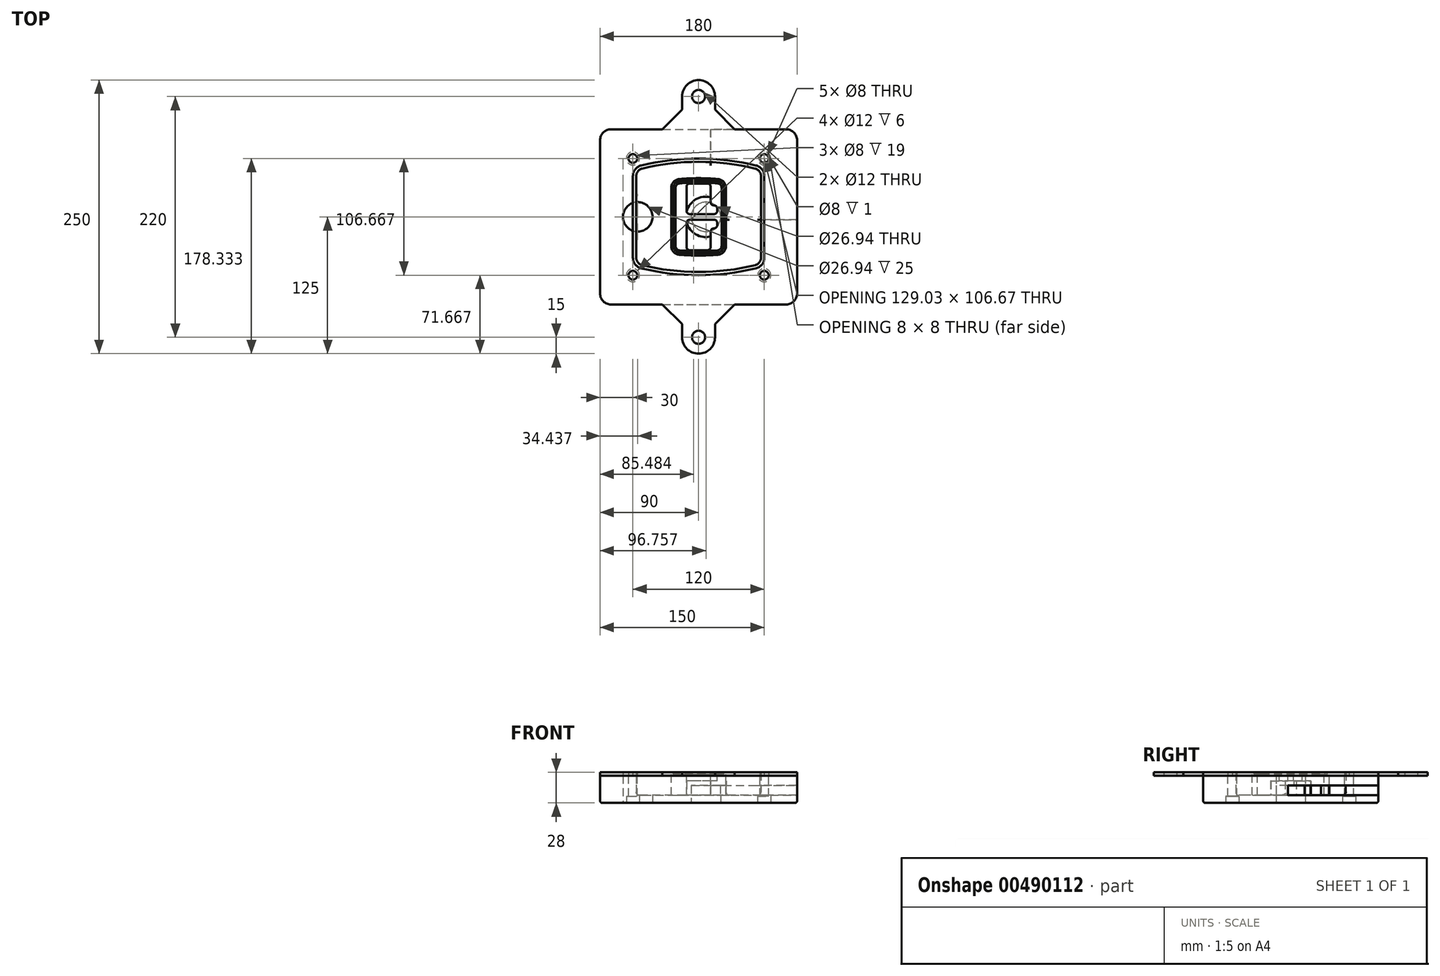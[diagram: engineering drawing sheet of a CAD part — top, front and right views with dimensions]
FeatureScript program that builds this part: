
annotation { "Feature Type Name" : "Feature", "Feature Type Description" : "" }
export const myFeature = defineFeature(function(context is Context, id is Id, definition is map)
    precondition{}
    {
        {
            var Q0;
            Q0=qCreatedBy(makeId("Top.planeOp"),FACE);
            var sketch = newSketch(context, id + "F0", { "sketchPlane" : qUnion([Q0])});
            skPoint(sketch, "E0.rect.middle", {"position": v(0, 0) * mm});
            skLineSegment(sketch, "E1.bottom", {"start": v(-80, -80) * mm, "end": v(80, -80) * mm});
            skLineSegment(sketch, "E1.top", {"start": v(-80, 80) * mm, "end": v(80, 80) * mm});
            skLineSegment(sketch, "E1.left", {"start": v(-90, -70) * mm, "end": v(-90, 70) * mm});
            skLineSegment(sketch, "E1.right", {"start": v(90, -70) * mm, "end": v(90, 70) * mm});
            skLineSegment(sketch, "E2", {"start": v(-90, 80) * mm, "end": v(90, -80) * mm, "construction": true});
            skLineSegment(sketch, "E3", {"start": v(90, 80) * mm, "end": v(-90, -80) * mm, "construction": true});
            skCircle(sketch, "E4", {"center": v(-60, 53.33) * mm, "radius": 4 * mm});
            skCircle(sketch, "E5", {"center": v(60, 53.33) * mm, "radius": 4 * mm});
            skCircle(sketch, "E6", {"center": v(60, -53.33) * mm, "radius": 4 * mm});
            skCircle(sketch, "E7", {"center": v(-60, -53.33) * mm, "radius": 4 * mm});
            skLineSegment(sketch, "E8", {"start": v(-60, 53.33) * mm, "end": v(60, 53.33) * mm, "construction": true});
            skLineSegment(sketch, "E9", {"start": v(60, 53.33) * mm, "end": v(60, -53.33) * mm, "construction": true});
            skLineSegment(sketch, "E10", {"start": v(60, -53.33) * mm, "end": v(-60, -53.33) * mm, "construction": true});
            skLineSegment(sketch, "E11", {"start": v(-60, -53.33) * mm, "end": v(-60, 53.33) * mm, "construction": true});
            skLineSegment(sketch, "E12", {"start": v(-60, 37.3) * mm, "end": v(-60, -37.3) * mm});
            skLineSegment(sketch, "E13", {"start": v(60, 37.3) * mm, "end": v(60, -37.3) * mm});
            skArc(sketch, "E14", {"start": v(52.38, 47.01) * mm, "mid": v(0, 53.33) * mm, "end": v(-52.38, 47.01) * mm});
            skArc(sketch, "E15", {"start": v(-52.38, -47.01) * mm, "mid": v(0, -53.33) * mm, "end": v(52.38, -47.01) * mm});
            skLineSegment(sketch, "E16", {"start": v(-60, 0) * mm, "end": v(60, 0) * mm, "construction": true});
            skPoint(sketch, "E17.visualSharp", {"position": v(-60, -45) * mm});
            skArc(sketch, "E17.filletArc", {"start": v(-60, -37.3) * mm, "mid": v(-57.87, -43.47) * mm, "end": v(-52.38, -47.01) * mm});
            skPoint(sketch, "E18.visualSharp", {"position": v(-60, 45) * mm});
            skArc(sketch, "E18.filletArc", {"start": v(-52.38, 47.01) * mm, "mid": v(-57.87, 43.47) * mm, "end": v(-60, 37.3) * mm});
            skPoint(sketch, "E19.visualSharp", {"position": v(60, 45) * mm});
            skArc(sketch, "E19.filletArc", {"start": v(60, 37.3) * mm, "mid": v(57.87, 43.47) * mm, "end": v(52.38, 47.01) * mm});
            skPoint(sketch, "E20.visualSharp", {"position": v(60, -45) * mm});
            skArc(sketch, "E20.filletArc", {"start": v(52.38, -47.01) * mm, "mid": v(57.87, -43.47) * mm, "end": v(60, -37.3) * mm});
            skPoint(sketch, "E21.visualSharp", {"position": v(-90, 80) * mm});
            skArc(sketch, "E21.filletArc", {"start": v(-80, 80) * mm, "mid": v(-87.07, 77.07) * mm, "end": v(-90, 70) * mm});
            skPoint(sketch, "E22.visualSharp", {"position": v(90, 80) * mm});
            skArc(sketch, "E22.filletArc", {"start": v(90, 70) * mm, "mid": v(87.07, 77.07) * mm, "end": v(80, 80) * mm});
            skPoint(sketch, "E23.visualSharp", {"position": v(90, -80) * mm});
            skArc(sketch, "E23.filletArc", {"start": v(80, -80) * mm, "mid": v(87.07, -77.07) * mm, "end": v(90, -70) * mm});
            skPoint(sketch, "E24.visualSharp", {"position": v(-90, -80) * mm});
            skArc(sketch, "E24.filletArc", {"start": v(-90, -70) * mm, "mid": v(-87.07, -77.07) * mm, "end": v(-80, -80) * mm});
            skArc(sketch, "E25.0", {"start": v(57, 37.3) * mm, "mid": v(55.5, 41.62) * mm, "end": v(51.67, 44.1) * mm});
            skLineSegment(sketch, "E25.1", {"start": v(57, 37.3) * mm, "end": v(57, -37.3) * mm});
            skArc(sketch, "E25.2", {"start": v(51.67, -44.1) * mm, "mid": v(55.5, -41.62) * mm, "end": v(57, -37.3) * mm});
            skArc(sketch, "E25.3", {"start": v(-51.67, -44.1) * mm, "mid": v(0, -50.33) * mm, "end": v(51.67, -44.1) * mm});
            skArc(sketch, "E25.4", {"start": v(-57, -37.3) * mm, "mid": v(-55.5, -41.62) * mm, "end": v(-51.67, -44.1) * mm});
            skArc(sketch, "E25.5", {"start": v(51.67, 44.1) * mm, "mid": v(0, 50.33) * mm, "end": v(-51.67, 44.1) * mm});
            skLineSegment(sketch, "E25.6", {"start": v(-57, 37.3) * mm, "end": v(-57, -37.3) * mm});
            skArc(sketch, "E25.7", {"start": v(-51.67, 44.1) * mm, "mid": v(-55.5, 41.62) * mm, "end": v(-57, 37.3) * mm});
            skArc(sketch, "E26.0", {"start": v(-53.33, 50.9) * mm, "mid": v(-61.01, 45.94) * mm, "end": v(-64, 37.3) * mm});
            skArc(sketch, "E26.1", {"start": v(53.33, 50.9) * mm, "mid": v(0, 57.33) * mm, "end": v(-53.33, 50.9) * mm});
            skArc(sketch, "E26.2", {"start": v(64, 37.3) * mm, "mid": v(61.01, 45.94) * mm, "end": v(53.33, 50.9) * mm});
            skLineSegment(sketch, "E26.3", {"start": v(64, 37.3) * mm, "end": v(64, -37.3) * mm});
            skArc(sketch, "E26.4", {"start": v(53.33, -50.9) * mm, "mid": v(61.01, -45.94) * mm, "end": v(64, -37.3) * mm});
            skLineSegment(sketch, "E26.5", {"start": v(-64, 37.3) * mm, "end": v(-64, -37.3) * mm});
            skArc(sketch, "E26.6", {"start": v(-53.33, -50.9) * mm, "mid": v(0, -57.33) * mm, "end": v(53.33, -50.9) * mm});
            skArc(sketch, "E26.7", {"start": v(-64, -37.3) * mm, "mid": v(-61.01, -45.94) * mm, "end": v(-53.33, -50.9) * mm});
            skSolve(sketch);
        }
        {
            var Q0;
            Q0=makeQuery(id+"F0.imprint","IMPRINT",FACE,{"disambiguationData":[TD([[makeQuery(id+"F0.imprint","IMPRINT",EDGE,{"derivedFrom":sQuery(id+"F0.wireOp",EDGE,"E1.bottom")}),1.0]])]});
            var Q1;
            Q1=makeQuery(id+"F0.imprint","IMPRINT",FACE,{"disambiguationData":[TD([[makeQuery(id+"F0.imprint","IMPRINT",EDGE,{"derivedFrom":sQuery(id+"F0.wireOp",EDGE,"E12")}),1.0]])]});
            var Q2;
            Q2=makeQuery(id+"F0.imprint","IMPRINT",FACE,{"disambiguationData":[TD([[makeQuery(id+"F0.imprint","IMPRINT",EDGE,{"derivedFrom":sQuery(id+"F0.wireOp",EDGE,"E25.0")}),1.0]])]});
            var Q3;
            Q3=makeQuery(id+"F0.imprint","IMPRINT",FACE,{"disambiguationData":[TD([[makeQuery(id+"F0.imprint","IMPRINT",EDGE,{"derivedFrom":sQuery(id+"F0.wireOp",EDGE,"E12")}),-1.0]])]});
            extrude(context, id + "F1", {"entities" : qUnion([Q0, Q1, Q2, Q3]), "oppositeDirection" : true, "depth" : 25 * mm});
        }
        {
            var Q0;
            Q0=makeQuery(id+"F0.imprint","IMPRINT",FACE,{"disambiguationData":[TD([[makeQuery(id+"F0.imprint","IMPRINT",EDGE,{"derivedFrom":sQuery(id+"F0.wireOp",EDGE,"E12")}),1.0]])]});
            extrude(context, id + "F2", {"entities" : qUnion([Q0]), "operationType" : NewBodyOperationType.ADD, "depth" : 3 * mm});
        }
        {
            var Q0;
            Q0=makeQuery(id+"F0.imprint","IMPRINT",FACE,{"disambiguationData":[TD([[makeQuery(id+"F0.imprint","IMPRINT",EDGE,{"derivedFrom":sQuery(id+"F0.wireOp",EDGE,"E25.0")}),1.0]])]});
            extrude(context, id + "F3", {"entities" : qUnion([Q0]), "operationType" : NewBodyOperationType.REMOVE, "oppositeDirection" : true, "depth" : 18 * mm});
        }
        {
            var Q0;
            Q0=makeQuery(id+"F2.opExtrude","CAP_FACE",FACE,{"disambiguationData":[OSD([sQuery(id+"F0.wireOp",EDGE,"E12"),sQuery(id+"F0.wireOp",EDGE,"E13"),sQuery(id+"F0.wireOp",EDGE,"E14"),sQuery(id+"F0.wireOp",EDGE,"E15"),sQuery(id+"F0.wireOp",EDGE,"E17.filletArc"),sQuery(id+"F0.wireOp",EDGE,"E18.filletArc"),sQuery(id+"F0.wireOp",EDGE,"E19.filletArc"),sQuery(id+"F0.wireOp",EDGE,"E20.filletArc"),sQuery(id+"F0.wireOp",EDGE,"E25.0"),sQuery(id+"F0.wireOp",EDGE,"E25.1"),sQuery(id+"F0.wireOp",EDGE,"E25.2"),sQuery(id+"F0.wireOp",EDGE,"E25.3"),sQuery(id+"F0.wireOp",EDGE,"E25.4"),sQuery(id+"F0.wireOp",EDGE,"E25.5"),sQuery(id+"F0.wireOp",EDGE,"E25.6"),sQuery(id+"F0.wireOp",EDGE,"E25.7")])],"isStart":false});
            var sketch = newSketch(context, id + "F4", { "sketchPlane" : qUnion([Q0])});
            skArc(sketch, "E27.0", {"start": v(-17.7, -34.56) * mm, "mid": v(0, -35.33) * mm, "end": v(17.7, -34.56) * mm});
            skArc(sketch, "E28.0", {"start": v(17.7, 34.56) * mm, "mid": v(0, 35.33) * mm, "end": v(-17.7, 34.56) * mm});
            skLineSegment(sketch, "E29", {"start": v(-25, 26.59) * mm, "end": v(-25, -26.59) * mm});
            skLineSegment(sketch, "E30", {"start": v(25, 26.59) * mm, "end": v(25, -26.59) * mm});
            skLineSegment(sketch, "E31", {"start": v(-25, 33.78) * mm, "end": v(25, 33.78) * mm, "construction": true});
            skLineSegment(sketch, "E32", {"start": v(-25, -33.78) * mm, "end": v(25, -33.78) * mm, "construction": true});
            skPoint(sketch, "E33.visualSharp", {"position": v(-25, 33.78) * mm});
            skArc(sketch, "E33.filletArc", {"start": v(-17.7, 34.56) * mm, "mid": v(-22.9, 32) * mm, "end": v(-25, 26.59) * mm});
            skPoint(sketch, "E34.visualSharp", {"position": v(25, 33.78) * mm});
            skArc(sketch, "E34.filletArc", {"start": v(25, 26.59) * mm, "mid": v(22.9, 32) * mm, "end": v(17.7, 34.56) * mm});
            skPoint(sketch, "E35.visualSharp", {"position": v(25, -33.78) * mm});
            skArc(sketch, "E35.filletArc", {"start": v(17.7, -34.56) * mm, "mid": v(22.9, -32) * mm, "end": v(25, -26.59) * mm});
            skPoint(sketch, "E36.visualSharp", {"position": v(-25, -33.78) * mm});
            skArc(sketch, "E36.filletArc", {"start": v(-25, -26.59) * mm, "mid": v(-22.9, -32) * mm, "end": v(-17.7, -34.56) * mm});
            skArc(sketch, "E37.0", {"start": v(51.67, 44.1) * mm, "mid": v(0, 50.33) * mm, "end": v(-51.67, 44.1) * mm});
            skArc(sketch, "E37.1", {"start": v(-51.67, 44.1) * mm, "mid": v(-55.5, 41.62) * mm, "end": v(-57, 37.3) * mm});
            skLineSegment(sketch, "E37.2", {"start": v(-57, 37.3) * mm, "end": v(-57, -37.3) * mm});
            skArc(sketch, "E37.3", {"start": v(-57, -37.3) * mm, "mid": v(-55.5, -41.62) * mm, "end": v(-51.67, -44.1) * mm});
            skArc(sketch, "E37.4", {"start": v(-51.67, -44.1) * mm, "mid": v(0, -50.33) * mm, "end": v(51.67, -44.1) * mm});
            skArc(sketch, "E37.5", {"start": v(51.67, -44.1) * mm, "mid": v(55.5, -41.62) * mm, "end": v(57, -37.3) * mm});
            skLineSegment(sketch, "E37.6", {"start": v(57, 37.3) * mm, "end": v(57, -37.3) * mm});
            skArc(sketch, "E37.7", {"start": v(57, 37.3) * mm, "mid": v(55.5, 41.62) * mm, "end": v(51.67, 44.1) * mm});
            skLineSegment(sketch, "E38.0", {"start": v(23, 26.59) * mm, "end": v(23, -26.59) * mm});
            skArc(sketch, "E38.1", {"start": v(17.53, -32.56) * mm, "mid": v(21.42, -30.64) * mm, "end": v(23, -26.59) * mm});
            skArc(sketch, "E38.2", {"start": v(-17.53, -32.56) * mm, "mid": v(0, -33.33) * mm, "end": v(17.53, -32.56) * mm});
            skArc(sketch, "E38.3", {"start": v(-23, -26.59) * mm, "mid": v(-21.42, -30.64) * mm, "end": v(-17.53, -32.56) * mm});
            skLineSegment(sketch, "E38.4", {"start": v(-23, 26.59) * mm, "end": v(-23, -26.59) * mm});
            skArc(sketch, "E38.5", {"start": v(23, 26.59) * mm, "mid": v(21.42, 30.64) * mm, "end": v(17.53, 32.56) * mm});
            skArc(sketch, "E38.6", {"start": v(-17.53, 32.56) * mm, "mid": v(-21.42, 30.64) * mm, "end": v(-23, 26.59) * mm});
            skArc(sketch, "E38.7", {"start": v(17.53, 32.56) * mm, "mid": v(0, 33.33) * mm, "end": v(-17.53, 32.56) * mm});
            skArc(sketch, "E39.0", {"start": v(21, 26.59) * mm, "mid": v(19.95, 29.29) * mm, "end": v(17.35, 30.57) * mm});
            skLineSegment(sketch, "E39.1", {"start": v(21, 26.59) * mm, "end": v(21, -26.59) * mm});
            skArc(sketch, "E39.2", {"start": v(17.35, -30.57) * mm, "mid": v(19.95, -29.29) * mm, "end": v(21, -26.59) * mm});
            skArc(sketch, "E39.3", {"start": v(-17.35, -30.57) * mm, "mid": v(0, -31.33) * mm, "end": v(17.35, -30.57) * mm});
            skArc(sketch, "E39.4", {"start": v(-21, -26.59) * mm, "mid": v(-19.95, -29.29) * mm, "end": v(-17.35, -30.57) * mm});
            skArc(sketch, "E39.5", {"start": v(17.35, 30.57) * mm, "mid": v(0, 31.33) * mm, "end": v(-17.35, 30.57) * mm});
            skLineSegment(sketch, "E39.6", {"start": v(-21, 26.59) * mm, "end": v(-21, -26.59) * mm});
            skArc(sketch, "E39.7", {"start": v(-17.35, 30.57) * mm, "mid": v(-19.95, 29.29) * mm, "end": v(-21, 26.59) * mm});
            skLineSegment(sketch, "E40", {"start": v(-25, 0) * mm, "end": v(25, 0) * mm, "construction": true});
            skLineSegment(sketch, "E41", {"start": v(-11, 5.5) * mm, "end": v(-11, 27.5) * mm});
            skLineSegment(sketch, "E42", {"start": v(-8, 30.5) * mm, "end": v(8, 30.5) * mm});
            skLineSegment(sketch, "E43", {"start": v(11, 27.5) * mm, "end": v(11, 13.5) * mm});
            skLineSegment(sketch, "E44", {"start": v(14, 10.5) * mm, "end": v(14, 10.5) * mm});
            skLineSegment(sketch, "E45", {"start": v(17, 7.5) * mm, "end": v(17, 5.5) * mm});
            skLineSegment(sketch, "E46", {"start": v(14, 2.5) * mm, "end": v(-8, 2.5) * mm});
            skPoint(sketch, "E47.visualSharp", {"position": v(-11, 30.5) * mm});
            skArc(sketch, "E47.filletArc", {"start": v(-8, 30.5) * mm, "mid": v(-10.12, 29.62) * mm, "end": v(-11, 27.5) * mm});
            skPoint(sketch, "E48.visualSharp", {"position": v(11, 30.5) * mm});
            skArc(sketch, "E48.filletArc", {"start": v(11, 27.5) * mm, "mid": v(10.12, 29.62) * mm, "end": v(8, 30.5) * mm});
            skPoint(sketch, "E49.visualSharp", {"position": v(11, 10.5) * mm});
            skArc(sketch, "E49.filletArc", {"start": v(11, 13.5) * mm, "mid": v(11.88, 11.38) * mm, "end": v(14, 10.5) * mm});
            skPoint(sketch, "E50.visualSharp", {"position": v(17, 10.5) * mm});
            skArc(sketch, "E50.filletArc", {"start": v(17, 7.5) * mm, "mid": v(16.12, 9.62) * mm, "end": v(14, 10.5) * mm});
            skPoint(sketch, "E51.visualSharp", {"position": v(17, 2.5) * mm});
            skArc(sketch, "E51.filletArc", {"start": v(14, 2.5) * mm, "mid": v(16.12, 3.38) * mm, "end": v(17, 5.5) * mm});
            skPoint(sketch, "E52.visualSharp", {"position": v(-11, 2.5) * mm});
            skArc(sketch, "E52.filletArc", {"start": v(-11, 5.5) * mm, "mid": v(-10.12, 3.38) * mm, "end": v(-8, 2.5) * mm});
            skLineSegment(sketch, "E53.0.MirrorCS", {"start": v(14, -2.5) * mm, "end": v(-8, -2.5) * mm});
            skArc(sketch, "E54.0.MirrorCS", {"start": v(-11, -5.5) * mm, "mid": v(-10.12, -3.38) * mm, "end": v(-8, -2.5) * mm});
            skLineSegment(sketch, "E55.0.MirrorCS", {"start": v(-11, -5.5) * mm, "end": v(-11, -27.5) * mm});
            skArc(sketch, "E56.0.MirrorCS", {"start": v(-8, -30.5) * mm, "mid": v(-10.12, -29.62) * mm, "end": v(-11, -27.5) * mm});
            skLineSegment(sketch, "E57.0.MirrorCS", {"start": v(-8, -30.5) * mm, "end": v(8, -30.5) * mm});
            skArc(sketch, "E58.0.MirrorCS", {"start": v(11, -27.5) * mm, "mid": v(10.12, -29.62) * mm, "end": v(8, -30.5) * mm});
            skLineSegment(sketch, "E59.0.MirrorCS", {"start": v(11, -27.5) * mm, "end": v(11, -13.5) * mm});
            skArc(sketch, "E60.0.MirrorCS", {"start": v(11, -13.5) * mm, "mid": v(11.88, -11.38) * mm, "end": v(14, -10.5) * mm});
            skArc(sketch, "E61.0.MirrorCS", {"start": v(17, -7.5) * mm, "mid": v(16.12, -9.62) * mm, "end": v(14, -10.5) * mm});
            skLineSegment(sketch, "E62.0.MirrorCS", {"start": v(17, -7.5) * mm, "end": v(17, -5.5) * mm});
            skArc(sketch, "E63.0.MirrorCS", {"start": v(14, -2.5) * mm, "mid": v(16.12, -3.38) * mm, "end": v(17, -5.5) * mm});
            skSolve(sketch);
        }
        {
            var Q0;
            Q0=makeQuery(id+"F4.imprint","IMPRINT",FACE,{"disambiguationData":[TD([[makeQuery(id+"F4.imprint","IMPRINT",EDGE,{"derivedFrom":sQuery(id+"F4.wireOp",EDGE,"E27.0")}),1.0]])]});
            var Q1;
            Q1=makeQuery(id+"F4.imprint","IMPRINT",FACE,{"disambiguationData":[TD([[makeQuery(id+"F4.imprint","IMPRINT",EDGE,{"derivedFrom":sQuery(id+"F4.wireOp",EDGE,"E38.0")}),-1.0]])]});
            var Q2;
            Q2=makeQuery(id+"F4.imprint","IMPRINT",FACE,{"disambiguationData":[TD([[makeQuery(id+"F4.imprint","IMPRINT",EDGE,{"derivedFrom":sQuery(id+"F4.wireOp",EDGE,"E39.0")}),1.0]])]});
            extrude(context, id + "F5", {"entities" : qUnion([Q0, Q1, Q2]), "operationType" : NewBodyOperationType.ADD, "endBound" : BoundingType.UP_TO_NEXT, "oppositeDirection" : true, "depth" : 25 * mm});
        }
        {
            var Q0;
            Q0=makeQuery(id+"F4.imprint","IMPRINT",FACE,{"disambiguationData":[TD([[makeQuery(id+"F4.imprint","IMPRINT",EDGE,{"derivedFrom":sQuery(id+"F4.wireOp",EDGE,"E38.0")}),-1.0]])]});
            extrude(context, id + "F6", {"entities" : qUnion([Q0]), "operationType" : NewBodyOperationType.REMOVE, "oppositeDirection" : true, "depth" : 2 * mm});
        }
        {
            var Q0;
            Q0=makeQuery(id+"F1.opExtrude","CAP_FACE",FACE,{"disambiguationData":[OSD([sQuery(id+"F0.wireOp",EDGE,"E1.bottom"),sQuery(id+"F0.wireOp",EDGE,"E1.top"),sQuery(id+"F0.wireOp",EDGE,"E1.left"),sQuery(id+"F0.wireOp",EDGE,"E1.right"),sQuery(id+"F0.wireOp",EDGE,"E4"),sQuery(id+"F0.wireOp",EDGE,"E5"),sQuery(id+"F0.wireOp",EDGE,"E6"),sQuery(id+"F0.wireOp",EDGE,"E7"),sQuery(id+"F0.wireOp",EDGE,"E21.filletArc"),sQuery(id+"F0.wireOp",EDGE,"E22.filletArc"),sQuery(id+"F0.wireOp",EDGE,"E23.filletArc"),sQuery(id+"F0.wireOp",EDGE,"E24.filletArc")])],"isStart":false});
            var sketch = newSketch(context, id + "F7", { "sketchPlane" : qUnion([Q0])});
            skCircle(sketch, "E64", {"center": v(6.76, 0) * mm, "radius": 13.47 * mm});
            skCircle(sketch, "E65", {"center": v(-55.56, 0) * mm, "radius": 13.47 * mm});
            skLineSegment(sketch, "E66", {"start": v(90, 0) * mm, "end": v(-90, 0) * mm});
            skCircle(sketch, "E67", {"center": v(6.76, 0) * mm, "radius": 18.47 * mm});
            skCircle(sketch, "E68", {"center": v(60, -53.33) * mm, "radius": 6 * mm});
            skCircle(sketch, "E69", {"center": v(-60, -53.33) * mm, "radius": 6 * mm});
            skCircle(sketch, "E70", {"center": v(-60, 53.33) * mm, "radius": 6 * mm});
            skCircle(sketch, "E71", {"center": v(60, 53.33) * mm, "radius": 6 * mm});
            skSolve(sketch);
        }
        {
            var Q0;
            {var subQ1=sQuery(id+"F7.wireOp",EDGE,"E66");var subQ4=sQuery(id+"F7.wireOp",EDGE,"E64");var subQ6=makeQuery(id+"F7.imprint","INTERSECT",VERTEX,{"disambiguationData":[OD(0.0)],"derivedFrom":[subQ4,subQ1]});Q0=makeQuery(id+"F7.imprint","IMPRINT",FACE,{"disambiguationData":[TD([[makeQuery(id+"F7.imprint","IMPRINT",EDGE,{"disambiguationData":[TD([[subQ6,-1.0]])],"derivedFrom":subQ4}),-1.0]])]});}
            var Q1;
            {var subQ0=sQuery(id+"F7.wireOp",EDGE,"E66");var subQ1=sQuery(id+"F7.wireOp",EDGE,"E64");var subQ3=makeQuery(id+"F7.imprint","INTERSECT",VERTEX,{"disambiguationData":[OD(0.0)],"derivedFrom":[subQ1,subQ0]});Q1=makeQuery(id+"F7.imprint","IMPRINT",FACE,{"disambiguationData":[TD([[makeQuery(id+"F7.imprint","IMPRINT",EDGE,{"disambiguationData":[TD([[subQ3,-1.0]])],"derivedFrom":subQ1}),1.0]])]});}
            var Q2;
            {var subQ0=sQuery(id+"F7.wireOp",EDGE,"E66");var subQ1=sQuery(id+"F7.wireOp",EDGE,"E64");var subQ3=makeQuery(id+"F7.imprint","INTERSECT",VERTEX,{"disambiguationData":[OD(0.0)],"derivedFrom":[subQ1,subQ0]});Q2=makeQuery(id+"F7.imprint","IMPRINT",FACE,{"disambiguationData":[TD([[makeQuery(id+"F7.imprint","IMPRINT",EDGE,{"disambiguationData":[TD([[subQ3,1.0]])],"derivedFrom":subQ1}),1.0]])]});}
            var Q3;
            {var subQ1=sQuery(id+"F7.wireOp",EDGE,"E66");var subQ4=sQuery(id+"F7.wireOp",EDGE,"E64");var subQ6=makeQuery(id+"F7.imprint","INTERSECT",VERTEX,{"disambiguationData":[OD(0.0)],"derivedFrom":[subQ4,subQ1]});Q3=makeQuery(id+"F7.imprint","IMPRINT",FACE,{"disambiguationData":[TD([[makeQuery(id+"F7.imprint","IMPRINT",EDGE,{"disambiguationData":[TD([[subQ6,1.0]])],"derivedFrom":subQ4}),-1.0]])]});}
            extrude(context, id + "F8", {"entities" : qUnion([Q0, Q1, Q2, Q3]), "operationType" : NewBodyOperationType.ADD, "oppositeDirection" : true, "depth" : 20 * mm});
        }
        {
            var Q0;
            {var subQ0=sQuery(id+"F7.wireOp",EDGE,"E66");var subQ1=sQuery(id+"F7.wireOp",EDGE,"E64");var subQ3=makeQuery(id+"F7.imprint","INTERSECT",VERTEX,{"disambiguationData":[OD(0.0)],"derivedFrom":[subQ1,subQ0]});Q0=makeQuery(id+"F7.imprint","IMPRINT",FACE,{"disambiguationData":[TD([[makeQuery(id+"F7.imprint","IMPRINT",EDGE,{"disambiguationData":[TD([[subQ3,-1.0]])],"derivedFrom":subQ1}),1.0]])]});}
            var Q1;
            {var subQ0=sQuery(id+"F7.wireOp",EDGE,"E66");var subQ1=sQuery(id+"F7.wireOp",EDGE,"E64");var subQ3=makeQuery(id+"F7.imprint","INTERSECT",VERTEX,{"disambiguationData":[OD(0.0)],"derivedFrom":[subQ1,subQ0]});Q1=makeQuery(id+"F7.imprint","IMPRINT",FACE,{"disambiguationData":[TD([[makeQuery(id+"F7.imprint","IMPRINT",EDGE,{"disambiguationData":[TD([[subQ3,1.0]])],"derivedFrom":subQ1}),1.0]])]});}
            extrude(context, id + "F9", {"entities" : qUnion([Q0, Q1]), "operationType" : NewBodyOperationType.REMOVE, "oppositeDirection" : true, "depth" : 16 * mm});
        }
        {
            var Q0;
            {var subQ0=sQuery(id+"F7.wireOp",EDGE,"E66");var subQ1=sQuery(id+"F7.wireOp",EDGE,"E65");var subQ3=makeQuery(id+"F7.imprint","INTERSECT",VERTEX,{"disambiguationData":[OD(0.0)],"derivedFrom":[subQ1,subQ0]});Q0=makeQuery(id+"F7.imprint","IMPRINT",FACE,{"disambiguationData":[TD([[makeQuery(id+"F7.imprint","IMPRINT",EDGE,{"disambiguationData":[TD([[subQ3,-1.0]])],"derivedFrom":subQ1}),1.0]])]});}
            var Q1;
            {var subQ0=sQuery(id+"F7.wireOp",EDGE,"E66");var subQ1=sQuery(id+"F7.wireOp",EDGE,"E65");var subQ3=makeQuery(id+"F7.imprint","INTERSECT",VERTEX,{"disambiguationData":[OD(0.0)],"derivedFrom":[subQ1,subQ0]});Q1=makeQuery(id+"F7.imprint","IMPRINT",FACE,{"disambiguationData":[TD([[makeQuery(id+"F7.imprint","IMPRINT",EDGE,{"disambiguationData":[TD([[subQ3,1.0]])],"derivedFrom":subQ1}),1.0]])]});}
            extrude(context, id + "F10", {"entities" : qUnion([Q0, Q1]), "operationType" : NewBodyOperationType.REMOVE, "oppositeDirection" : true, "depth" : 25 * mm});
        }
        {
            var Q0;
            Q0=makeQuery(id+"F7.imprint","IMPRINT",FACE,{"disambiguationData":[TD([[makeQuery(id+"F7.imprint","IMPRINT",EDGE,{"derivedFrom":sQuery(id+"F7.wireOp",EDGE,"E68")}),1.0]])]});
            var Q1;
            Q1=makeQuery(id+"F7.imprint","IMPRINT",FACE,{"disambiguationData":[TD([[makeQuery(id+"F7.imprint","IMPRINT",EDGE,{"derivedFrom":makeQuery(id+"F1.opExtrude","CAP_EDGE",EDGE,{"disambiguationData":[OSD([sQuery(id+"F0.wireOp",EDGE,"E5")])],"isStart":false})}),-1.0]])]});
            var Q2;
            Q2=makeQuery(id+"F7.imprint","IMPRINT",FACE,{"disambiguationData":[TD([[makeQuery(id+"F7.imprint","IMPRINT",EDGE,{"derivedFrom":sQuery(id+"F7.wireOp",EDGE,"E69")}),1.0]])]});
            var Q3;
            Q3=makeQuery(id+"F7.imprint","IMPRINT",FACE,{"disambiguationData":[TD([[makeQuery(id+"F7.imprint","IMPRINT",EDGE,{"derivedFrom":makeQuery(id+"F1.opExtrude","CAP_EDGE",EDGE,{"disambiguationData":[OSD([sQuery(id+"F0.wireOp",EDGE,"E4")])],"isStart":false})}),-1.0]])]});
            var Q4;
            Q4=makeQuery(id+"F7.imprint","IMPRINT",FACE,{"disambiguationData":[TD([[makeQuery(id+"F7.imprint","IMPRINT",EDGE,{"derivedFrom":sQuery(id+"F7.wireOp",EDGE,"E70")}),1.0]])]});
            var Q5;
            Q5=makeQuery(id+"F7.imprint","IMPRINT",FACE,{"disambiguationData":[TD([[makeQuery(id+"F7.imprint","IMPRINT",EDGE,{"derivedFrom":makeQuery(id+"F1.opExtrude","CAP_EDGE",EDGE,{"disambiguationData":[OSD([sQuery(id+"F0.wireOp",EDGE,"E7")])],"isStart":false})}),-1.0]])]});
            var Q6;
            Q6=makeQuery(id+"F7.imprint","IMPRINT",FACE,{"disambiguationData":[TD([[makeQuery(id+"F7.imprint","IMPRINT",EDGE,{"derivedFrom":sQuery(id+"F7.wireOp",EDGE,"E71")}),1.0]])]});
            var Q7;
            Q7=makeQuery(id+"F7.imprint","IMPRINT",FACE,{"disambiguationData":[TD([[makeQuery(id+"F7.imprint","IMPRINT",EDGE,{"derivedFrom":makeQuery(id+"F1.opExtrude","CAP_EDGE",EDGE,{"disambiguationData":[OSD([sQuery(id+"F0.wireOp",EDGE,"E6")])],"isStart":false})}),-1.0]])]});
            extrude(context, id + "F11", {"entities" : qUnion([Q0, Q1, Q2, Q3, Q4, Q5, Q6, Q7]), "operationType" : NewBodyOperationType.REMOVE, "oppositeDirection" : true, "depth" : 6 * mm});
        }
        {
            var Q0;
            Q0=makeQuery(id+"F9.boolean.opBoolean","COPY",FACE,{"derivedFrom":makeQuery(id+"F9.opExtrude","CAP_FACE",FACE,{"disambiguationData":[OSD([sQuery(id+"F7.wireOp",EDGE,"E64")])],"isStart":false})});
            var sketch = newSketch(context, id + "F12", { "sketchPlane" : qUnion([Q0])});
            skArc(sketch, "E72.0", {"start": v(11, -88.19) * mm, "mid": v(97.1, -83.6) * mm, "end": v(92.5, 2.5) * mm});
            skLineSegment(sketch, "E72.1", {"start": v(11, -17.97) * mm, "end": v(11, -17.97) * mm});
            skLineSegment(sketch, "E73", {"start": v(92.5, -105.13) * mm, "end": v(102.3, -105.13) * mm});
            skLineSegment(sketch, "E74.0", {"start": v(92.5, 2.5) * mm, "end": v(14, 2.5) * mm});
            skArc(sketch, "E74.1", {"start": v(14, 2.5) * mm, "mid": v(16.12, 3.38) * mm, "end": v(17, 5.5) * mm});
            skLineSegment(sketch, "E74.2", {"start": v(17, 7.5) * mm, "end": v(17, 5.5) * mm});
            skArc(sketch, "E74.3", {"start": v(17, 7.5) * mm, "mid": v(16.12, 9.62) * mm, "end": v(14, 10.5) * mm});
            skArc(sketch, "E74.4", {"start": v(11, 13.5) * mm, "mid": v(11.88, 11.38) * mm, "end": v(14, 10.5) * mm});
            skLineSegment(sketch, "E74.5", {"start": v(11, 13.5) * mm, "end": v(11, -88.19) * mm});
            skLineSegment(sketch, "E74.7", {"start": v(92.5, -2.5) * mm, "end": v(14, -2.5) * mm});
            skArc(sketch, "E74.8", {"start": v(14, -2.5) * mm, "mid": v(16.12, -3.38) * mm, "end": v(17, -5.5) * mm});
            skLineSegment(sketch, "E74.9", {"start": v(17, -7.5) * mm, "end": v(17, -5.5) * mm});
            skArc(sketch, "E74.10", {"start": v(17, -7.5) * mm, "mid": v(16.12, -9.62) * mm, "end": v(14, -10.5) * mm});
            skArc(sketch, "E74.11", {"start": v(11, -13.5) * mm, "mid": v(11.88, -11.38) * mm, "end": v(14, -10.5) * mm});
            skLineSegment(sketch, "E74.12", {"start": v(11, -17.97) * mm, "end": v(11, -13.5) * mm});
            skPoint(sketch, "E75.orphan", {"position": v(11, -27.5) * mm});
            skPoint(sketch, "E76.orphan", {"position": v(-8, -2.5) * mm});
            skPoint(sketch, "E77.orphan", {"position": v(-8, 2.5) * mm});
            skPoint(sketch, "E78.orphan", {"position": v(11, 27.5) * mm});
            skSolve(sketch);
        }
        {
            var Q0;
            {var subQ7=sQuery(id+"F12.wireOp",EDGE,"E72.0");var subQ14=sQuery(id+"F12.wireOp",EDGE,"E72.1");var subQ16=sQuery(id+"F12.wireOp",EDGE,"E74.1");var subQ18=sQuery(id+"F12.wireOp",EDGE,"E74.8");Q0=qUnion([makeQuery(id+"F12.imprint","IMPRINT",FACE,{"disambiguationData":[TD([[makeQuery(id+"F12.imprint","IMPRINT",EDGE,{"derivedFrom":subQ7}),1.0]])]}),makeQuery(id+"F12.imprint","IMPRINT",FACE,{"disambiguationData":[TD([[makeQuery(id+"F12.imprint","IMPRINT",EDGE,{"derivedFrom":subQ14}),1.0]])]}),makeQuery(id+"F12.imprint","IMPRINT",FACE,{"disambiguationData":[TD([[makeQuery(id+"F12.imprint","IMPRINT",EDGE,{"derivedFrom":subQ16}),1.0]])]}),makeQuery(id+"F12.imprint","IMPRINT",FACE,{"disambiguationData":[TD([[makeQuery(id+"F12.imprint","IMPRINT",EDGE,{"derivedFrom":subQ18}),-1.0]])]})]);}
            var Q1;
            Q1=makeQuery(id+"F5.boolean.opBoolean","SPLIT",FACE,{"disambiguationData":[TD([makeQuery(id+"F5.opExtrude","SWEPT_FACE",FACE,{"disambiguationData":[OSD([sQuery(id+"F4.wireOp",EDGE,"E41")])]})])],"derivedFrom":makeQuery(id+"F3.boolean.opBoolean","COPY",FACE,{"derivedFrom":makeQuery(id+"F3.opExtrude","CAP_FACE",FACE,{"disambiguationData":[OSD([sQuery(id+"F0.wireOp",EDGE,"E25.0"),sQuery(id+"F0.wireOp",EDGE,"E25.1"),sQuery(id+"F0.wireOp",EDGE,"E25.2"),sQuery(id+"F0.wireOp",EDGE,"E25.3"),sQuery(id+"F0.wireOp",EDGE,"E25.4"),sQuery(id+"F0.wireOp",EDGE,"E25.5"),sQuery(id+"F0.wireOp",EDGE,"E25.6"),sQuery(id+"F0.wireOp",EDGE,"E25.7")])],"isStart":false})})});
            extrude(context, id + "F13", {"entities" : qUnion([Q0]), "operationType" : NewBodyOperationType.REMOVE, "endBound" : BoundingType.UP_TO_SURFACE, "endBoundEntityFace" : qUnion([Q1]), "depth" : 25 * mm});
        }
        {
            var Q0;
            Q0=makeQuery(id+"F3.boolean.opBoolean","COPY",EDGE,{"derivedFrom":makeQuery(id+"F3.opExtrude","CAP_EDGE",EDGE,{"disambiguationData":[OSD([sQuery(id+"F0.wireOp",EDGE,"E25.6")])],"isStart":false})});
            var Q1;
            Q1=makeQuery(id+"F8.boolean.opBoolean","INTERSECT",EDGE,{"derivedFrom":[makeQuery(id+"F5.opExtrude","SWEPT_FACE",FACE,{"disambiguationData":[OSD([sQuery(id+"F4.wireOp",EDGE,"E30")])]}),makeQuery(id+"F8.opExtrude","CAP_FACE",FACE,{"disambiguationData":[OSD([sQuery(id+"F7.wireOp",EDGE,"E67")])],"isStart":false})]});
            var Q2;
            Q2=makeQuery(id+"F8.boolean.opBoolean","INTERSECT",EDGE,{"disambiguationData":[OD(1.0)],"derivedFrom":[makeQuery(id+"F5.opExtrude","SWEPT_FACE",FACE,{"disambiguationData":[OSD([sQuery(id+"F4.wireOp",EDGE,"E30")])]}),makeQuery(id+"F8.opExtrude","SWEPT_FACE",FACE,{"disambiguationData":[OSD([sQuery(id+"F7.wireOp",EDGE,"E67")])]})]});
            var Q3;
            {var subQ0=makeQuery(id+"F3.boolean.opBoolean","COPY",FACE,{"derivedFrom":makeQuery(id+"F3.opExtrude","CAP_FACE",FACE,{"disambiguationData":[OSD([sQuery(id+"F0.wireOp",EDGE,"E25.0"),sQuery(id+"F0.wireOp",EDGE,"E25.1"),sQuery(id+"F0.wireOp",EDGE,"E25.2"),sQuery(id+"F0.wireOp",EDGE,"E25.3"),sQuery(id+"F0.wireOp",EDGE,"E25.4"),sQuery(id+"F0.wireOp",EDGE,"E25.5"),sQuery(id+"F0.wireOp",EDGE,"E25.6"),sQuery(id+"F0.wireOp",EDGE,"E25.7")])],"isStart":false})});var subQ1=sQuery(id+"F4.wireOp",EDGE,"E30");Q3=makeQuery(id+"F8.boolean.opBoolean","SPLIT",EDGE,{"disambiguationData":[TD([makeQuery(id+"F5.opExtrude","SWEPT_FACE",FACE,{"disambiguationData":[OSD([sQuery(id+"F4.wireOp",EDGE,"E35.filletArc")])]})])],"derivedFrom":makeQuery(id+"F5.opExtrude","TWEAK_EDGE",EDGE,{"derivedFrom":[subQ0,makeQuery(id+"F4.imprint","IMPRINT",EDGE,{"derivedFrom":subQ1})]})});}
            var Q4;
            {var subQ0=sQuery(id+"F0.wireOp",EDGE,"E25.0");var subQ1=sQuery(id+"F0.wireOp",EDGE,"E25.1");var subQ2=sQuery(id+"F0.wireOp",EDGE,"E25.2");var subQ3=sQuery(id+"F0.wireOp",EDGE,"E25.3");var subQ4=sQuery(id+"F0.wireOp",EDGE,"E25.4");var subQ5=sQuery(id+"F0.wireOp",EDGE,"E25.5");var subQ6=sQuery(id+"F0.wireOp",EDGE,"E25.6");var subQ7=sQuery(id+"F0.wireOp",EDGE,"E25.7");Q4=makeQuery(id+"F8.boolean.opBoolean","INTERSECT",EDGE,{"derivedFrom":[makeQuery(id+"F5.boolean.opBoolean","SPLIT",FACE,{"disambiguationData":[TD([makeQuery(id+"F2.opExtrude","SWEPT_FACE",FACE,{"disambiguationData":[OSD([subQ0])]})])],"derivedFrom":makeQuery(id+"F3.boolean.opBoolean","COPY",FACE,{"derivedFrom":makeQuery(id+"F3.opExtrude","CAP_FACE",FACE,{"disambiguationData":[OSD([subQ0,subQ1,subQ2,subQ3,subQ4,subQ5,subQ6,subQ7])],"isStart":false})})}),makeQuery(id+"F8.opExtrude","SWEPT_FACE",FACE,{"disambiguationData":[OSD([sQuery(id+"F7.wireOp",EDGE,"E67")])]})]});}
            var Q5;
            Q5=makeQuery(id+"F8.boolean.opBoolean","INTERSECT",EDGE,{"disambiguationData":[OD(0.0)],"derivedFrom":[makeQuery(id+"F5.opExtrude","SWEPT_FACE",FACE,{"disambiguationData":[OSD([sQuery(id+"F4.wireOp",EDGE,"E30")])]}),makeQuery(id+"F8.opExtrude","SWEPT_FACE",FACE,{"disambiguationData":[OSD([sQuery(id+"F7.wireOp",EDGE,"E67")])]})]});
            fillet(context, id + "F14", {"entities" : qUnion([Q0, Q1, Q2, Q3, Q4, Q5]), "radius" : 3 * mm, "tangentPropagation" : true, "allowEdgeOverflow" : false});
        }
        {
            var Q0;
            Q0=makeQuery(id+"F1.opExtrude","CAP_EDGE",EDGE,{"disambiguationData":[OSD([sQuery(id+"F0.wireOp",EDGE,"E1.bottom")])],"isStart":false});
            fillet(context, id + "F15", {"entities" : qUnion([Q0]), "radius" : 2 * mm, "tangentPropagation" : true, "allowEdgeOverflow" : false});
        }
        {
            var Q0;
            {var subQ0=sQuery(id+"F0.wireOp",EDGE,"E21.filletArc");var subQ1=sQuery(id+"F0.wireOp",EDGE,"E7");var subQ2=sQuery(id+"F0.wireOp",EDGE,"E6");var subQ3=sQuery(id+"F0.wireOp",EDGE,"E5");var subQ4=sQuery(id+"F0.wireOp",EDGE,"E4");var subQ5=sQuery(id+"F0.wireOp",EDGE,"E22.filletArc");var subQ6=sQuery(id+"F0.wireOp",EDGE,"E1.bottom");var subQ7=sQuery(id+"F0.wireOp",EDGE,"E1.right");var subQ8=sQuery(id+"F0.wireOp",EDGE,"E1.top");var subQ9=sQuery(id+"F0.wireOp",EDGE,"E1.left");var subQ10=sQuery(id+"F0.wireOp",EDGE,"E23.filletArc");var subQ11=sQuery(id+"F0.wireOp",EDGE,"E24.filletArc");Q0=makeQuery(id+"F2.boolean.opBoolean","SPLIT",FACE,{"disambiguationData":[TD([makeQuery(id+"F1.opExtrude","SWEPT_FACE",FACE,{"disambiguationData":[OSD([subQ6])]})])],"derivedFrom":makeQuery(id+"F1.opExtrude","CAP_FACE",FACE,{"disambiguationData":[OSD([subQ6,subQ8,subQ9,subQ7,subQ4,subQ3,subQ2,subQ1,subQ0,subQ5,subQ10,subQ11])],"isStart":true})});}
            var sketch = newSketch(context, id + "F16", { "sketchPlane" : qUnion([Q0])});
            skLineSegment(sketch, "E79", {"start": v(0, 80) * mm, "end": v(0, 110) * mm, "construction": true});
            skPoint(sketch, "E79.endSnap0", {"position": v(0, 80) * mm});
            skCircle(sketch, "E80", {"center": v(0, 110) * mm, "radius": 6 * mm});
            skArc(sketch, "E81", {"start": v(-15, 110) * mm, "mid": v(0, 125) * mm, "end": v(15, 110) * mm});
            skLineSegment(sketch, "E82", {"start": v(-15, 110) * mm, "end": v(-15, 98) * mm});
            skLineSegment(sketch, "E83", {"start": v(-15, 98) * mm, "end": v(-33, 80) * mm});
            skLineSegment(sketch, "E84", {"start": v(15, 110) * mm, "end": v(15, 98) * mm});
            skLineSegment(sketch, "E85", {"start": v(15, 98) * mm, "end": v(33, 80) * mm});
            skLineSegment(sketch, "E86", {"start": v(-90, 0) * mm, "end": v(90, 0) * mm, "construction": true});
            skLineSegment(sketch, "E87.MirrorCS", {"start": v(15, -110) * mm, "end": v(15, -98) * mm});
            skLineSegment(sketch, "E88.MirrorCS", {"start": v(-15, -110) * mm, "end": v(-15, -98) * mm});
            skPoint(sketch, "E89.MirrorP", {"position": v(0, -80) * mm});
            skArc(sketch, "E90.MirrorCS", {"start": v(-15, -110) * mm, "mid": v(0, -125) * mm, "end": v(15, -110) * mm});
            skLineSegment(sketch, "E91.MirrorCS", {"start": v(0, -80) * mm, "end": v(0, -110) * mm, "construction": true});
            skLineSegment(sketch, "E92.MirrorCS", {"start": v(15, -98) * mm, "end": v(33, -80) * mm});
            skCircle(sketch, "E93.MirrorC", {"center": v(0, -110) * mm, "radius": 6 * mm});
            skLineSegment(sketch, "E94.MirrorCS", {"start": v(-15, -98) * mm, "end": v(-33, -80) * mm});
            skSolve(sketch);
        }
        {
            var Q0;
            Q0=makeQuery(id+"F16.imprint","IMPRINT",FACE,{"disambiguationData":[TD([[makeQuery(id+"F16.imprint","IMPRINT",EDGE,{"derivedFrom":makeQuery(id+"F1.opExtrude","CAP_EDGE",EDGE,{"disambiguationData":[OSD([sQuery(id+"F0.wireOp",EDGE,"E1.left")])],"isStart":true})}),-1.0]])]});
            var Q1;
            Q1=makeQuery(id+"F16.imprint","IMPRINT",FACE,{"disambiguationData":[TD([[makeQuery(id+"F16.imprint","IMPRINT",EDGE,{"derivedFrom":sQuery(id+"F16.wireOp",EDGE,"E80")}),-1.0]])]});
            var Q2;
            Q2=makeQuery(id+"F16.imprint","IMPRINT",FACE,{"disambiguationData":[TD([[makeQuery(id+"F16.imprint","IMPRINT",EDGE,{"derivedFrom":sQuery(id+"F16.wireOp",EDGE,"E87.MirrorCS")}),1.0]])]});
            var Q3;
            Q3=makeQuery(id+"F2.opExtrude","CAP_FACE",FACE,{"disambiguationData":[OSD([sQuery(id+"F0.wireOp",EDGE,"E12"),sQuery(id+"F0.wireOp",EDGE,"E13"),sQuery(id+"F0.wireOp",EDGE,"E14"),sQuery(id+"F0.wireOp",EDGE,"E15"),sQuery(id+"F0.wireOp",EDGE,"E17.filletArc"),sQuery(id+"F0.wireOp",EDGE,"E18.filletArc"),sQuery(id+"F0.wireOp",EDGE,"E19.filletArc"),sQuery(id+"F0.wireOp",EDGE,"E20.filletArc"),sQuery(id+"F0.wireOp",EDGE,"E25.0"),sQuery(id+"F0.wireOp",EDGE,"E25.1"),sQuery(id+"F0.wireOp",EDGE,"E25.2"),sQuery(id+"F0.wireOp",EDGE,"E25.3"),sQuery(id+"F0.wireOp",EDGE,"E25.4"),sQuery(id+"F0.wireOp",EDGE,"E25.5"),sQuery(id+"F0.wireOp",EDGE,"E25.6"),sQuery(id+"F0.wireOp",EDGE,"E25.7")])],"isStart":false});
            extrude(context, id + "F17", {"entities" : qUnion([Q0, Q1, Q2]), "endBound" : BoundingType.UP_TO_SURFACE, "endBoundEntityFace" : qUnion([Q3]), "depth" : 25 * mm});
        }
    });
